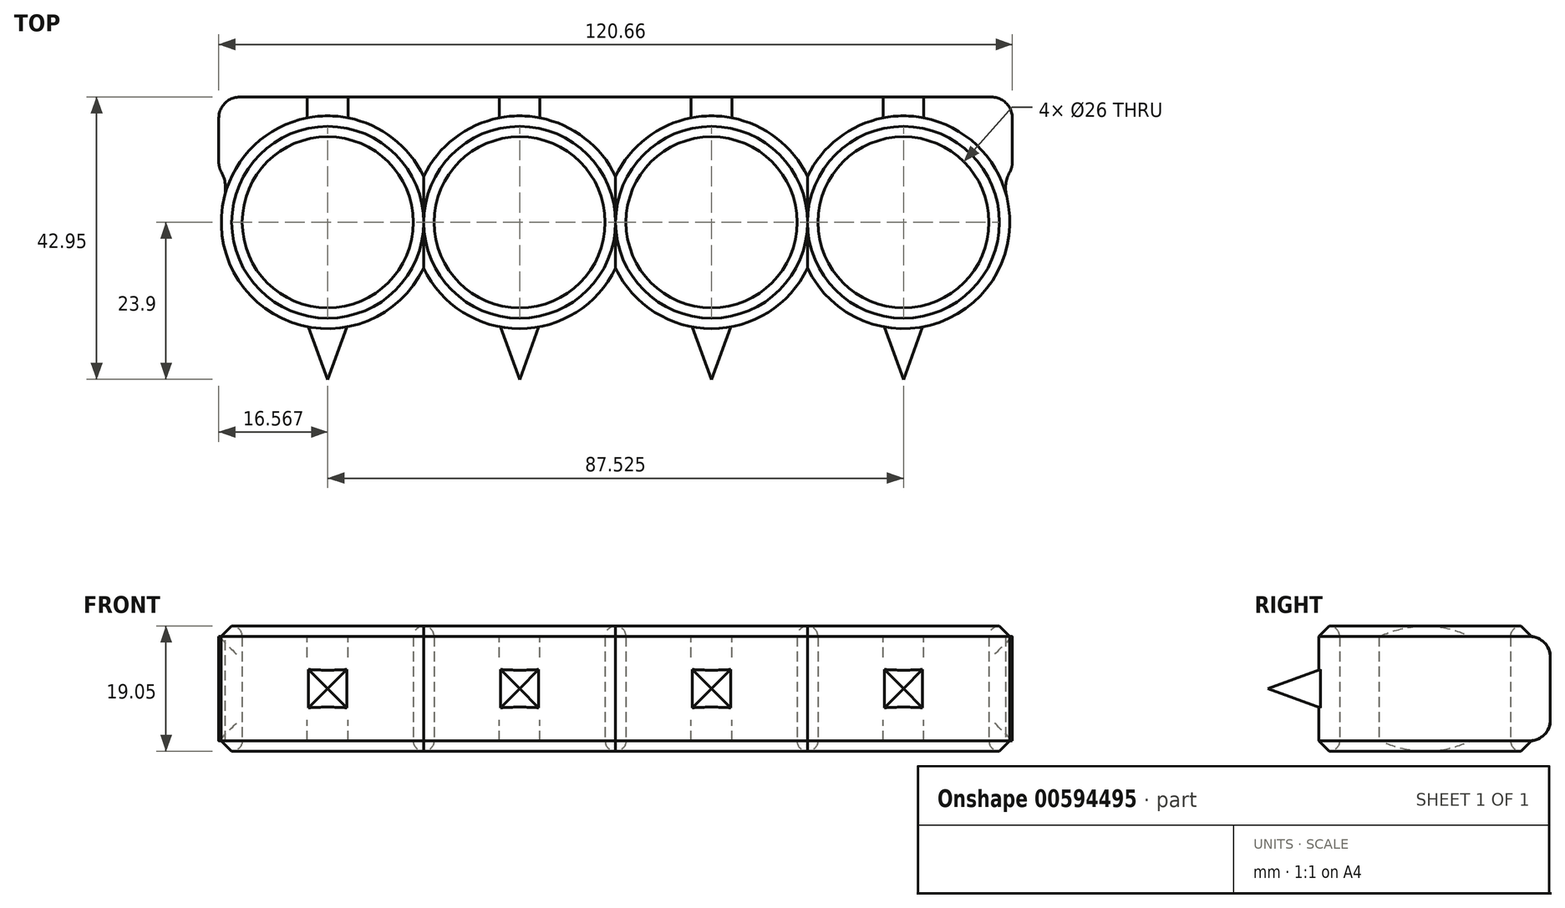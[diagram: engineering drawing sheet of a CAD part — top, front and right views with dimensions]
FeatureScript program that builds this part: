
annotation { "Feature Type Name" : "Feature", "Feature Type Description" : "" }
export const myFeature = defineFeature(function(context is Context, id is Id, definition is map)
    precondition{}
    {
        {
            var Q0;
            Q0=qCreatedBy(makeId("Top.planeOp"),FACE);
            var sketch = newSketch(context, id + "F0", { "sketchPlane" : qUnion([Q0])});
            skCircle(sketch, "E0", {"center": v(-14.59, 0) * mm, "radius": 13 * mm});
            skCircle(sketch, "E1", {"center": v(-43.76, 0) * mm, "radius": 13 * mm});
            skCircle(sketch, "E2", {"center": v(14.59, 0) * mm, "radius": 13 * mm});
            skCircle(sketch, "E3", {"center": v(43.76, 0) * mm, "radius": 13 * mm});
            skCircle(sketch, "E4", {"center": v(-43.76, 0) * mm, "radius": 16.18 * mm});
            skCircle(sketch, "E5", {"center": v(-14.59, 0) * mm, "radius": 16.18 * mm});
            skCircle(sketch, "E6", {"center": v(14.59, 0) * mm, "radius": 16.18 * mm});
            skCircle(sketch, "E7", {"center": v(43.76, 0) * mm, "radius": 16.18 * mm});
            skSolve(sketch);
        }
        {
            var Q0;
            Q0 = qSketchRegion(id + "F0", true);
            extrude(context, id + "F1", {"entities" : qUnion([Q0]), "depth" : 19.05 * mm, "offsetDistance" : 25.4 * mm});
        }
        {
            var Q0;
            {var subQ0=sQuery(id+"F0.wireOp",EDGE,"E5");Q0=makeQuery(id+"F1.opExtrude","CAP_EDGE",EDGE,{"disambiguationData":[OSD([subQ0]),TDD([makeQuery(id+"F0.imprint","IMPRINT",EDGE,{"disambiguationData":[TD([[makeQuery(id+"F0.imprint","INTERSECT",VERTEX,{"disambiguationData":[OD(1.0)],"derivedFrom":[sQuery(id+"F0.wireOp",EDGE,"E4"),subQ0]}),-1.0]])],"derivedFrom":subQ0})])],"isStart":false});}
            var Q1;
            Q1=makeQuery(id+"F1.opExtrude","CAP_EDGE",EDGE,{"disambiguationData":[OSD([sQuery(id+"F0.wireOp",EDGE,"E4")])],"isStart":false});
            var Q2;
            {var subQ0=sQuery(id+"F0.wireOp",EDGE,"E5");Q2=makeQuery(id+"F1.opExtrude","CAP_EDGE",EDGE,{"disambiguationData":[OSD([subQ0]),TDD([makeQuery(id+"F0.imprint","IMPRINT",EDGE,{"disambiguationData":[TD([[makeQuery(id+"F0.imprint","INTERSECT",VERTEX,{"disambiguationData":[OD(0.0)],"derivedFrom":[sQuery(id+"F0.wireOp",EDGE,"E4"),subQ0]}),1.0]])],"derivedFrom":subQ0})])],"isStart":false});}
            var Q3;
            {var subQ0=sQuery(id+"F0.wireOp",EDGE,"E6");Q3=makeQuery(id+"F1.opExtrude","CAP_EDGE",EDGE,{"disambiguationData":[OSD([subQ0]),TDD([makeQuery(id+"F0.imprint","IMPRINT",EDGE,{"disambiguationData":[TD([[makeQuery(id+"F0.imprint","INTERSECT",VERTEX,{"disambiguationData":[OD(0.0)],"derivedFrom":[sQuery(id+"F0.wireOp",EDGE,"E5"),subQ0]}),1.0]])],"derivedFrom":subQ0})])],"isStart":false});}
            var Q4;
            {var subQ0=sQuery(id+"F0.wireOp",EDGE,"E6");Q4=makeQuery(id+"F1.opExtrude","CAP_EDGE",EDGE,{"disambiguationData":[OSD([subQ0]),TDD([makeQuery(id+"F0.imprint","IMPRINT",EDGE,{"disambiguationData":[TD([[makeQuery(id+"F0.imprint","INTERSECT",VERTEX,{"disambiguationData":[OD(1.0)],"derivedFrom":[sQuery(id+"F0.wireOp",EDGE,"E5"),subQ0]}),-1.0]])],"derivedFrom":subQ0})])],"isStart":false});}
            var Q5;
            Q5=makeQuery(id+"F1.opExtrude","CAP_EDGE",EDGE,{"disambiguationData":[OSD([sQuery(id+"F0.wireOp",EDGE,"E7")])],"isStart":false});
            var Q6;
            Q6=makeQuery(id+"F1.opExtrude","CAP_EDGE",EDGE,{"disambiguationData":[OSD([sQuery(id+"F0.wireOp",EDGE,"E4")])],"isStart":true});
            var Q7;
            {var subQ0=sQuery(id+"F0.wireOp",EDGE,"E5");Q7=makeQuery(id+"F1.opExtrude","CAP_EDGE",EDGE,{"disambiguationData":[OSD([subQ0]),TDD([makeQuery(id+"F0.imprint","IMPRINT",EDGE,{"disambiguationData":[TD([[makeQuery(id+"F0.imprint","INTERSECT",VERTEX,{"disambiguationData":[OD(1.0)],"derivedFrom":[sQuery(id+"F0.wireOp",EDGE,"E4"),subQ0]}),-1.0]])],"derivedFrom":subQ0})])],"isStart":true});}
            var Q8;
            {var subQ0=sQuery(id+"F0.wireOp",EDGE,"E6");Q8=makeQuery(id+"F1.opExtrude","CAP_EDGE",EDGE,{"disambiguationData":[OSD([subQ0]),TDD([makeQuery(id+"F0.imprint","IMPRINT",EDGE,{"disambiguationData":[TD([[makeQuery(id+"F0.imprint","INTERSECT",VERTEX,{"disambiguationData":[OD(1.0)],"derivedFrom":[sQuery(id+"F0.wireOp",EDGE,"E5"),subQ0]}),-1.0]])],"derivedFrom":subQ0})])],"isStart":true});}
            var Q9;
            Q9=makeQuery(id+"F1.opExtrude","CAP_EDGE",EDGE,{"disambiguationData":[OSD([sQuery(id+"F0.wireOp",EDGE,"E7")])],"isStart":true});
            var Q10;
            {var subQ0=sQuery(id+"F0.wireOp",EDGE,"E6");Q10=makeQuery(id+"F1.opExtrude","CAP_EDGE",EDGE,{"disambiguationData":[OSD([subQ0]),TDD([makeQuery(id+"F0.imprint","IMPRINT",EDGE,{"disambiguationData":[TD([[makeQuery(id+"F0.imprint","INTERSECT",VERTEX,{"disambiguationData":[OD(0.0)],"derivedFrom":[sQuery(id+"F0.wireOp",EDGE,"E5"),subQ0]}),1.0]])],"derivedFrom":subQ0})])],"isStart":true});}
            var Q11;
            {var subQ0=sQuery(id+"F0.wireOp",EDGE,"E5");Q11=makeQuery(id+"F1.opExtrude","CAP_EDGE",EDGE,{"disambiguationData":[OSD([subQ0]),TDD([makeQuery(id+"F0.imprint","IMPRINT",EDGE,{"disambiguationData":[TD([[makeQuery(id+"F0.imprint","INTERSECT",VERTEX,{"disambiguationData":[OD(0.0)],"derivedFrom":[sQuery(id+"F0.wireOp",EDGE,"E4"),subQ0]}),1.0]])],"derivedFrom":subQ0})])],"isStart":true});}
            chamfer(context, id + "F2", {"entities" : qUnion([Q0, Q1, Q2, Q3, Q4, Q5, Q6, Q7, Q8, Q9, Q10, Q11]), "width" : 1.59 * mm, "tangentPropagation" : true});
        }
        {
            var Q0;
            Q0=makeQuery(id+"F1.opExtrude","SWEPT_FACE",FACE,{"disambiguationData":[OSD([sQuery(id+"F0.wireOp",EDGE,"E3")])]});
            var Q1;
            Q1=makeQuery(id+"F1.opExtrude","SWEPT_FACE",FACE,{"disambiguationData":[OSD([sQuery(id+"F0.wireOp",EDGE,"E2")])]});
            var Q2;
            Q2=makeQuery(id+"F1.opExtrude","SWEPT_FACE",FACE,{"disambiguationData":[OSD([sQuery(id+"F0.wireOp",EDGE,"E0")])]});
            var Q3;
            Q3=makeQuery(id+"F1.opExtrude","SWEPT_FACE",FACE,{"disambiguationData":[OSD([sQuery(id+"F0.wireOp",EDGE,"E1")])]});
            fillet(context, id + "F3", {"entities" : qUnion([Q0, Q1, Q2, Q3]), "radius" : 1.59 * mm, "tangentPropagation" : true, "allowEdgeOverflow" : false});
        }
        {
            var Q0;
            Q0=qCreatedBy(makeId("Front.planeOp"),FACE);
            cPlane(context, id + "F4", {"entities" : qUnion([Q0]), "cplaneType" : CPlaneType.OFFSET, "offset" : 13 * mm, "width" : 152.4 * mm, "height" : 152.4 * mm});
        }
        {
            var Q0;
            Q0=qCreatedBy(id+"F4.planeOp",FACE);
            var sketch = newSketch(context, id + "F5", { "sketchPlane" : qUnion([Q0])});
            skLineSegment(sketch, "E8.bottom", {"start": v(-47.73, 5.56) * mm, "end": v(-39.8, 5.56) * mm});
            skLineSegment(sketch, "E8.top", {"start": v(-47.73, 13.5) * mm, "end": v(-39.8, 13.5) * mm});
            skLineSegment(sketch, "E8.left", {"start": v(-47.73, 5.56) * mm, "end": v(-47.73, 13.5) * mm});
            skLineSegment(sketch, "E8.right", {"start": v(-39.8, 5.56) * mm, "end": v(-39.8, 13.5) * mm});
            skPoint(sketch, "E8.middle", {"position": v(-43.76, 9.53) * mm});
            skLineSegment(sketch, "E9.bottom", {"start": v(-18.56, 5.56) * mm, "end": v(-10.62, 5.56) * mm});
            skLineSegment(sketch, "E9.top", {"start": v(-18.56, 13.5) * mm, "end": v(-10.62, 13.5) * mm});
            skLineSegment(sketch, "E9.left", {"start": v(-18.56, 5.56) * mm, "end": v(-18.56, 13.5) * mm});
            skLineSegment(sketch, "E9.right", {"start": v(-10.62, 5.56) * mm, "end": v(-10.62, 13.5) * mm});
            skPoint(sketch, "E9.middle", {"position": v(-14.59, 9.53) * mm});
            skLineSegment(sketch, "E10.bottom", {"start": v(10.62, 5.56) * mm, "end": v(18.56, 5.56) * mm});
            skLineSegment(sketch, "E10.top", {"start": v(10.62, 13.5) * mm, "end": v(18.56, 13.5) * mm});
            skLineSegment(sketch, "E10.left", {"start": v(10.62, 5.56) * mm, "end": v(10.62, 13.5) * mm});
            skLineSegment(sketch, "E10.right", {"start": v(18.56, 5.56) * mm, "end": v(18.56, 13.5) * mm});
            skPoint(sketch, "E10.middle", {"position": v(14.59, 9.52) * mm});
            skLineSegment(sketch, "E11.bottom", {"start": v(39.8, 5.56) * mm, "end": v(47.73, 5.56) * mm});
            skLineSegment(sketch, "E11.top", {"start": v(39.8, 13.5) * mm, "end": v(47.73, 13.5) * mm});
            skLineSegment(sketch, "E11.left", {"start": v(39.8, 5.56) * mm, "end": v(39.8, 13.5) * mm});
            skLineSegment(sketch, "E11.right", {"start": v(47.73, 5.56) * mm, "end": v(47.73, 13.5) * mm});
            skPoint(sketch, "E11.middle", {"position": v(43.76, 9.52) * mm});
            skSolve(sketch);
        }
        {
            var Q0;
            Q0 = qSketchRegion(id + "F5", true);
            extrude(context, id + "F6", {"entities" : qUnion([Q0]), "operationType" : NewBodyOperationType.ADD, "depth" : 12.7 * mm, "offsetDistance" : 25.4 * mm, "hasDraft" : true, "draftAngle" : 20 * degree, "draftPullDirection" : true});
        }
        {
            var Q0;
            Q0=qCreatedBy(makeId("Front.planeOp"),FACE);
            cPlane(context, id + "F7", {"entities" : qUnion([Q0]), "cplaneType" : CPlaneType.OFFSET, "offset" : 19.05 * mm, "oppositeDirection" : true, "width" : 152.4 * mm, "height" : 152.4 * mm});
        }
        {
            var Q0;
            Q0=qCreatedBy(id+"F7.planeOp",FACE);
            var sketch = newSketch(context, id + "F8", { "sketchPlane" : qUnion([Q0])});
            skLineSegment(sketch, "E12.bottom", {"start": v(60.33, 17.46) * mm, "end": v(-60.33, 17.46) * mm});
            skLineSegment(sketch, "E12.top", {"start": v(60.33, 1.59) * mm, "end": v(-60.33, 1.59) * mm});
            skLineSegment(sketch, "E12.left", {"start": v(60.33, 17.46) * mm, "end": v(60.33, 1.59) * mm});
            skLineSegment(sketch, "E12.right", {"start": v(-60.33, 17.46) * mm, "end": v(-60.33, 1.59) * mm});
            skPoint(sketch, "E12.middle", {"position": v(0, 9.53) * mm});
            skSolve(sketch);
        }
        {
            var Q0;
            Q0 = qSketchRegion(id + "F8", true);
            extrude(context, id + "F9", {"entities" : qUnion([Q0]), "operationType" : NewBodyOperationType.ADD, "depth" : 12.7 * mm, "offsetDistance" : 25.4 * mm});
        }
        {
            var Q0;
            {var subQ0=sQuery(id+"F0.wireOp",EDGE,"E3");var subQ1=sQuery(id+"F8.wireOp",EDGE,"E12.bottom");Q0=makeQuery(id+"F9.boolean.opBoolean","SPLIT",FACE,{"disambiguationData":[TD([makeQuery(id+"F1.opExtrude","SWEPT_FACE",FACE,{"disambiguationData":[OSD([subQ0])]})])],"derivedFrom":makeQuery(id+"F9.opExtrude","SWEPT_FACE",FACE,{"disambiguationData":[OSD([subQ1])]})});}
            var Q1;
            {var subQ0=sQuery(id+"F0.wireOp",EDGE,"E2");var subQ1=sQuery(id+"F8.wireOp",EDGE,"E12.bottom");Q1=makeQuery(id+"F9.boolean.opBoolean","SPLIT",FACE,{"disambiguationData":[TD([makeQuery(id+"F1.opExtrude","SWEPT_FACE",FACE,{"disambiguationData":[OSD([subQ0])]})])],"derivedFrom":makeQuery(id+"F9.opExtrude","SWEPT_FACE",FACE,{"disambiguationData":[OSD([subQ1])]})});}
            var Q2;
            {var subQ0=sQuery(id+"F0.wireOp",EDGE,"E0");var subQ1=sQuery(id+"F8.wireOp",EDGE,"E12.bottom");Q2=makeQuery(id+"F9.boolean.opBoolean","SPLIT",FACE,{"disambiguationData":[TD([makeQuery(id+"F1.opExtrude","SWEPT_FACE",FACE,{"disambiguationData":[OSD([subQ0])]})])],"derivedFrom":makeQuery(id+"F9.opExtrude","SWEPT_FACE",FACE,{"disambiguationData":[OSD([subQ1])]})});}
            var Q3;
            {var subQ0=sQuery(id+"F0.wireOp",EDGE,"E1");var subQ1=sQuery(id+"F8.wireOp",EDGE,"E12.bottom");Q3=makeQuery(id+"F9.boolean.opBoolean","SPLIT",FACE,{"disambiguationData":[TD([makeQuery(id+"F1.opExtrude","SWEPT_FACE",FACE,{"disambiguationData":[OSD([subQ0])]})])],"derivedFrom":makeQuery(id+"F9.opExtrude","SWEPT_FACE",FACE,{"disambiguationData":[OSD([subQ1])]})});}
            extrude(context, id + "F10", {"entities" : qUnion([Q0, Q1, Q2, Q3]), "operationType" : NewBodyOperationType.REMOVE, "oppositeDirection" : true, "depth" : 25.4 * mm, "offsetDistance" : 25.4 * mm});
        }
        {
            var Q0;
            Q0=makeQuery(id+"F9.opExtrude","CAP_EDGE",EDGE,{"disambiguationData":[OSD([sQuery(id+"F8.wireOp",EDGE,"E12.left")])],"isStart":true});
            var Q1;
            Q1=makeQuery(id+"F9.opExtrude","CAP_EDGE",EDGE,{"disambiguationData":[OSD([sQuery(id+"F8.wireOp",EDGE,"E12.right")])],"isStart":true});
            var Q2;
            Q2=makeQuery(id+"F9.opExtrude","CAP_EDGE",EDGE,{"disambiguationData":[OSD([sQuery(id+"F8.wireOp",EDGE,"E12.bottom")])],"isStart":true});
            var Q3;
            Q3=makeQuery(id+"F9.opExtrude","CAP_EDGE",EDGE,{"disambiguationData":[OSD([sQuery(id+"F8.wireOp",EDGE,"E12.top")])],"isStart":true});
            var Q4;
            Q4=makeQuery(id+"F9.opExtrude","CAP_EDGE",EDGE,{"disambiguationData":[OSD([sQuery(id+"F8.wireOp",EDGE,"E12.left")])],"isStart":false});
            var Q5;
            Q5=makeQuery(id+"F9.opExtrude","CAP_EDGE",EDGE,{"disambiguationData":[OSD([sQuery(id+"F8.wireOp",EDGE,"E12.right")])],"isStart":false});
            fillet(context, id + "F11", {"entities" : qUnion([Q0, Q1, Q2, Q3, Q4, Q5]), "radius" : 3.17 * mm, "tangentPropagation" : true, "allowEdgeOverflow" : false});
        }
        {
            var Q0;
            Q0=makeQuery(id+"F11.opFillet","BLEND_EDGE",EDGE,{"blendedFrom":[makeQuery(id+"F9.opExtrude","CAP_EDGE",EDGE,{"disambiguationData":[OSD([sQuery(id+"F8.wireOp",EDGE,"E12.left")])],"isStart":false}),makeQuery(id+"F1.opExtrude","SWEPT_FACE",FACE,{"disambiguationData":[OSD([sQuery(id+"F0.wireOp",EDGE,"E7")])]})],"blendedInto":[makeQuery(id+"F1.opExtrude","SWEPT_FACE",FACE,{"disambiguationData":[OSD([sQuery(id+"F0.wireOp",EDGE,"E7")])]})]});
            var Q1;
            Q1=makeQuery(id+"F11.opFillet","BLEND_EDGE",EDGE,{"blendedFrom":[makeQuery(id+"F9.opExtrude","CAP_EDGE",EDGE,{"disambiguationData":[OSD([sQuery(id+"F8.wireOp",EDGE,"E12.right")])],"isStart":false}),makeQuery(id+"F1.opExtrude","SWEPT_FACE",FACE,{"disambiguationData":[OSD([sQuery(id+"F0.wireOp",EDGE,"E4")])]})],"blendedInto":[makeQuery(id+"F1.opExtrude","SWEPT_FACE",FACE,{"disambiguationData":[OSD([sQuery(id+"F0.wireOp",EDGE,"E4")])]})]});
            fillet(context, id + "F12", {"entities" : qUnion([Q0, Q1]), "radius" : 5.08 * mm, "tangentPropagation" : true, "allowEdgeOverflow" : false});
        }
    });
